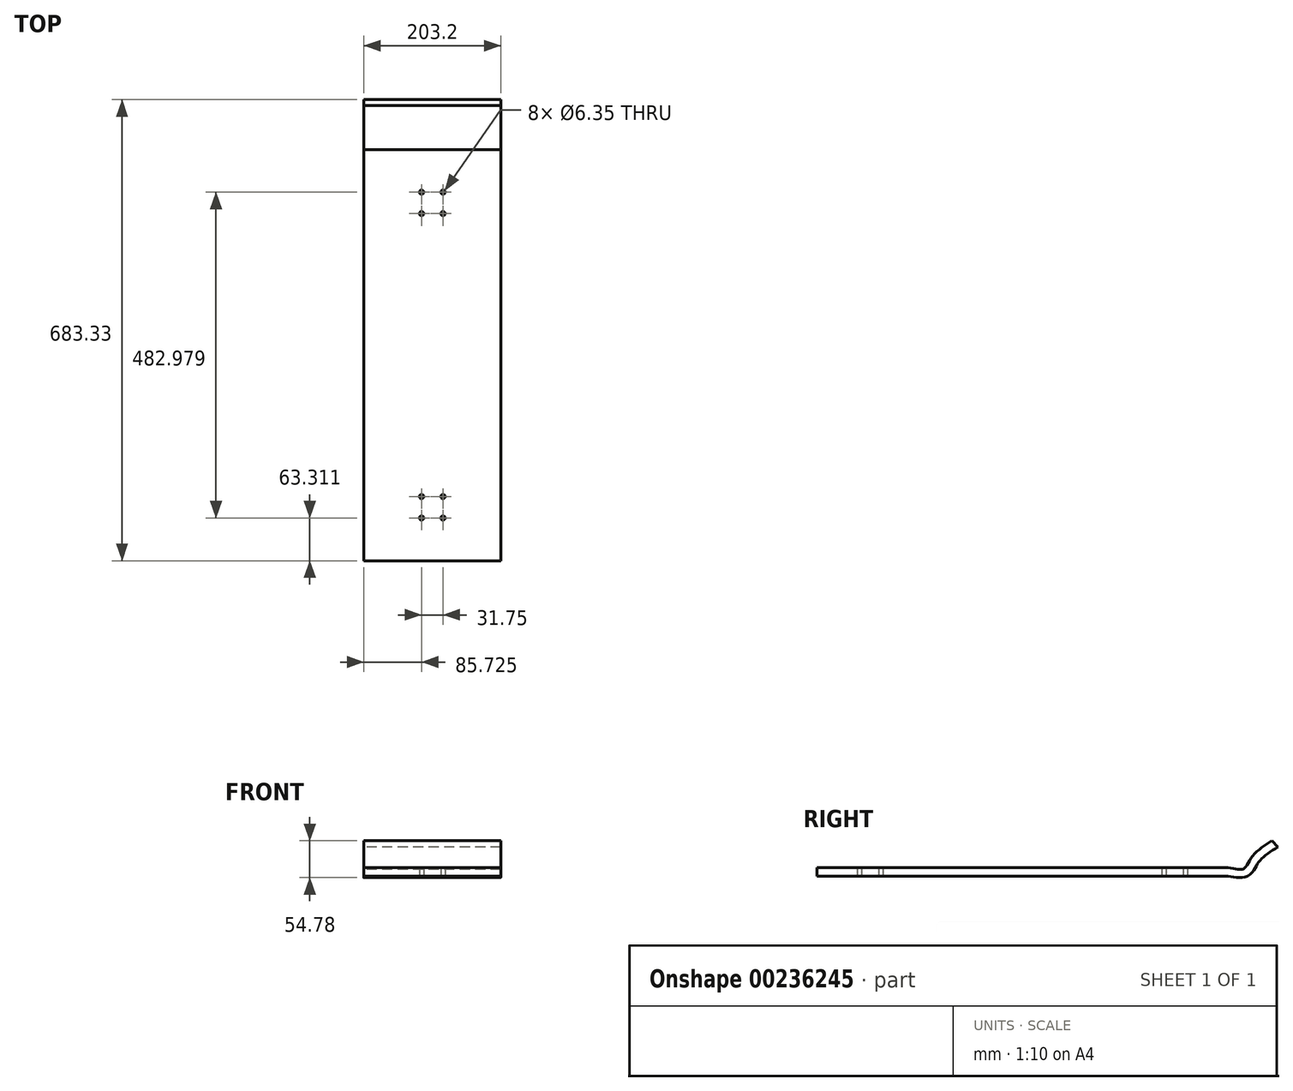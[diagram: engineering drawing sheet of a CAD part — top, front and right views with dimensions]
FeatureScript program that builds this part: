
annotation { "Feature Type Name" : "Feature", "Feature Type Description" : "" }
export const myFeature = defineFeature(function(context is Context, id is Id, definition is map)
    precondition{}
    {
        {
            var Q0;
            Q0=qCreatedBy(makeId("Top.planeOp"),FACE);
            var sketch = newSketch(context, id + "F0", { "sketchPlane" : qUnion([Q0])});
            skLineSegment(sketch, "E0.bottom", {"start": v(101.6, 304.8) * mm, "end": v(-101.6, 304.8) * mm});
            skLineSegment(sketch, "E0.top", {"start": v(101.6, -304.8) * mm, "end": v(-101.6, -304.8) * mm});
            skLineSegment(sketch, "E0.left", {"start": v(101.6, 304.8) * mm, "end": v(101.6, -304.8) * mm});
            skLineSegment(sketch, "E0.right", {"start": v(-101.6, 304.8) * mm, "end": v(-101.6, -304.8) * mm});
            skPoint(sketch, "E0.middle", {"position": v(0, 0) * mm});
            skPoint(sketch, "E1.middle", {"position": v(0, 225.61) * mm});
            skCircle(sketch, "E2", {"center": v(-15.87, 241.49) * mm, "radius": 3.18 * mm});
            skCircle(sketch, "E3", {"center": v(15.88, 241.49) * mm, "radius": 3.18 * mm});
            skCircle(sketch, "E4", {"center": v(-15.87, 209.74) * mm, "radius": 3.18 * mm});
            skCircle(sketch, "E5", {"center": v(15.88, 209.74) * mm, "radius": 3.18 * mm});
            skPoint(sketch, "E1.left.start.orphan", {"position": v(25.4, 251.01) * mm});
            skPoint(sketch, "E1.right.start.orphan", {"position": v(-25.4, 251.01) * mm});
            skPoint(sketch, "E1.top.end.orphan", {"position": v(-25.4, 200.21) * mm});
            skPoint(sketch, "E1.top.start.orphan", {"position": v(25.4, 200.21) * mm});
            skCircle(sketch, "E6.MirrorC", {"center": v(-15.87, -209.74) * mm, "radius": 3.18 * mm});
            skCircle(sketch, "E7.MirrorC", {"center": v(15.88, -209.74) * mm, "radius": 3.18 * mm});
            skCircle(sketch, "E8.MirrorC", {"center": v(15.88, -241.49) * mm, "radius": 3.18 * mm});
            skCircle(sketch, "E9.MirrorC", {"center": v(-15.87, -241.49) * mm, "radius": 3.18 * mm});
            skSolve(sketch);
        }
        {
            var Q0;
            Q0=makeQuery(id+"F0.imprint","IMPRINT",FACE,{"disambiguationData":[TD([[makeQuery(id+"F0.imprint","IMPRINT",EDGE,{"derivedFrom":sQuery(id+"F0.wireOp",EDGE,"E0.bottom")}),1.0]])]});
            extrude(context, id + "F1", {"entities" : qUnion([Q0]), "endBound" : BoundingType.SYMMETRIC, "depth" : 12.7 * mm});
        }
        {
            var Q0;
            Q0=qCreatedBy(makeId("Right.planeOp"),FACE);
            var sketch = newSketch(context, id + "F2", { "sketchPlane" : qUnion([Q0])});
            skFitSpline(sketch, "E10", {"points": [v(306.2, 0) * mm, v(331.58, 0) * mm, v(345.67, 19.22) * mm, v(375.27, 42.48) * mm], "startDerivative": vector(92, -17.11) * mm, "endDerivative": vector(89.12, 55.59) * mm});
            skSolve(sketch);
        }
        {
            var Q0;
            Q0=makeQuery(id+"F1.opExtrude","SWEPT_FACE",FACE,{"disambiguationData":[OSD([sQuery(id+"F0.wireOp",EDGE,"E0.bottom")])]});
            var Q1;
            Q1=sQuery(id+"F2.wireOp",EDGE,"E10");
            sweep(context, id + "F3", {"operationType" : NewBodyOperationType.ADD, "profiles" : qUnion([Q0]), "path" : qUnion([Q1])});
        }
    });
